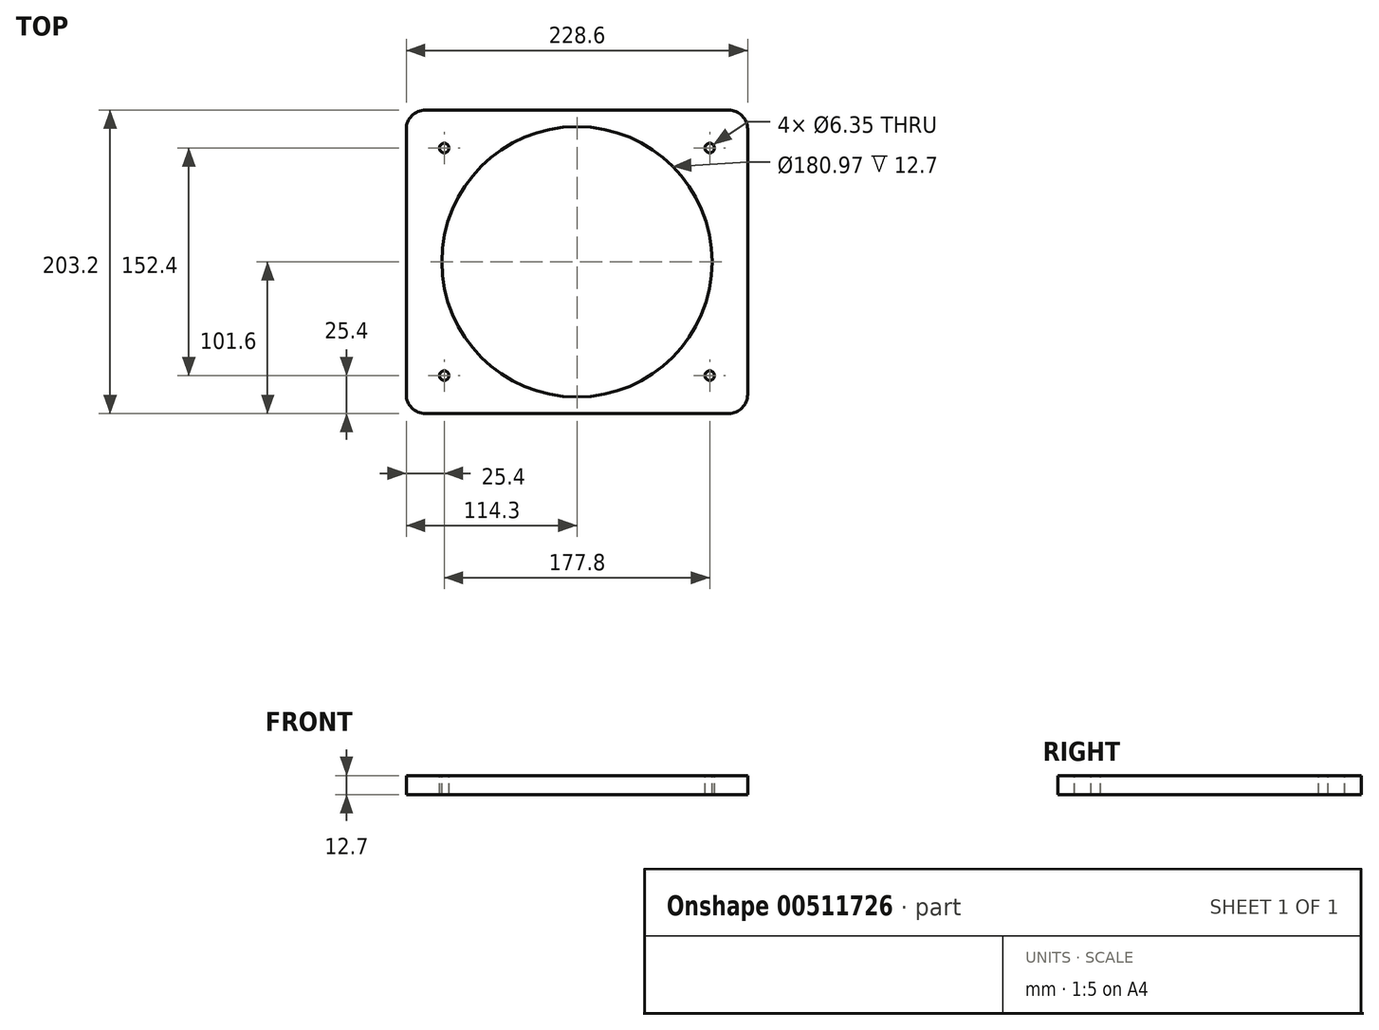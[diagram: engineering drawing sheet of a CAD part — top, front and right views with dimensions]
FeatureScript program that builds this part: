
annotation { "Feature Type Name" : "Feature", "Feature Type Description" : "" }
export const myFeature = defineFeature(function(context is Context, id is Id, definition is map)
    precondition{}
    {
        {
            var Q0;
            Q0=qCreatedBy(makeId("Top.planeOp"),FACE);
            var sketch = newSketch(context, id + "F0", { "sketchPlane" : qUnion([Q0])});
            skLineSegment(sketch, "E0.bottom", {"start": v(-101.6, 101.6) * mm, "end": v(101.6, 101.6) * mm});
            skLineSegment(sketch, "E0.top", {"start": v(-101.6, -101.6) * mm, "end": v(101.6, -101.6) * mm});
            skLineSegment(sketch, "E0.left", {"start": v(-114.3, 88.9) * mm, "end": v(-114.3, -88.9) * mm});
            skLineSegment(sketch, "E0.right", {"start": v(114.3, 88.9) * mm, "end": v(114.3, -88.9) * mm});
            skPoint(sketch, "E0.middle", {"position": v(0, 0) * mm});
            skPoint(sketch, "E1.visualSharp", {"position": v(-114.3, 101.6) * mm});
            skArc(sketch, "E1.filletArc", {"start": v(-101.6, 101.6) * mm, "mid": v(-110.58, 97.88) * mm, "end": v(-114.3, 88.9) * mm});
            skPoint(sketch, "E2.visualSharp", {"position": v(114.3, 101.6) * mm});
            skArc(sketch, "E2.filletArc", {"start": v(114.3, 88.9) * mm, "mid": v(110.58, 97.88) * mm, "end": v(101.6, 101.6) * mm});
            skPoint(sketch, "E3.visualSharp", {"position": v(-114.3, -101.6) * mm});
            skArc(sketch, "E3.filletArc", {"start": v(-114.3, -88.9) * mm, "mid": v(-110.58, -97.88) * mm, "end": v(-101.6, -101.6) * mm});
            skPoint(sketch, "E4.visualSharp", {"position": v(114.3, -101.6) * mm});
            skArc(sketch, "E4.filletArc", {"start": v(101.6, -101.6) * mm, "mid": v(110.58, -97.88) * mm, "end": v(114.3, -88.9) * mm});
            skSolve(sketch);
        }
        {
            var Q0;
            Q0=makeQuery(id+"F0.imprint","IMPRINT",FACE,{"disambiguationData":[TD([[makeQuery(id+"F0.imprint","IMPRINT",EDGE,{"derivedFrom":sQuery(id+"F0.wireOp",EDGE,"E0.bottom")}),-1.0]])]});
            extrude(context, id + "F1", {"entities" : qUnion([Q0]), "depth" : 12.7 * mm});
        }
        {
            var Q0;
            Q0=makeQuery(id+"F1.opExtrude","CAP_FACE",FACE,{"disambiguationData":[OSD([sQuery(id+"F0.wireOp",EDGE,"E0.bottom"),sQuery(id+"F0.wireOp",EDGE,"E0.top"),sQuery(id+"F0.wireOp",EDGE,"E0.left"),sQuery(id+"F0.wireOp",EDGE,"E0.right"),sQuery(id+"F0.wireOp",EDGE,"E1.filletArc"),sQuery(id+"F0.wireOp",EDGE,"E2.filletArc"),sQuery(id+"F0.wireOp",EDGE,"E3.filletArc"),sQuery(id+"F0.wireOp",EDGE,"E4.filletArc")])],"isStart":false});
            var sketch = newSketch(context, id + "F2", { "sketchPlane" : qUnion([Q0])});
            skCircle(sketch, "E5", {"center": v(0, 0) * mm, "radius": 90.49 * mm});
            skSolve(sketch);
        }
        {
            var Q0;
            Q0 = qSketchRegion(id + "F2", true);
            extrude(context, id + "F3", {"entities" : qUnion([Q0]), "operationType" : NewBodyOperationType.REMOVE, "oppositeDirection" : true, "depth" : 12.7 * mm});
        }
        {
            var Q0;
            Q0=makeQuery(id+"F1.opExtrude","CAP_FACE",FACE,{"disambiguationData":[OSD([sQuery(id+"F0.wireOp",EDGE,"E0.bottom"),sQuery(id+"F0.wireOp",EDGE,"E0.top"),sQuery(id+"F0.wireOp",EDGE,"E0.left"),sQuery(id+"F0.wireOp",EDGE,"E0.right"),sQuery(id+"F0.wireOp",EDGE,"E1.filletArc"),sQuery(id+"F0.wireOp",EDGE,"E2.filletArc"),sQuery(id+"F0.wireOp",EDGE,"E3.filletArc"),sQuery(id+"F0.wireOp",EDGE,"E4.filletArc")])],"isStart":false});
            var sketch = newSketch(context, id + "F4", { "sketchPlane" : qUnion([Q0])});
            skCircle(sketch, "E6", {"center": v(-88.9, -76.2) * mm, "radius": 2.54 * mm});
            skCircle(sketch, "E7.0.1.0", {"center": v(-88.9, 76.2) * mm, "radius": 2.54 * mm});
            skCircle(sketch, "E7.1.0.0", {"center": v(88.9, -76.2) * mm, "radius": 2.54 * mm});
            skCircle(sketch, "E7.1.1.0", {"center": v(88.9, 76.2) * mm, "radius": 2.54 * mm});
            skLineSegment(sketch, "E7.direction1", {"start": v(-88.9, -76.2) * mm, "end": v(88.9, -76.2) * mm, "construction": true});
            skLineSegment(sketch, "E7.direction2", {"start": v(-88.9, -76.2) * mm, "end": v(-88.9, 76.2) * mm, "construction": true});
            skSolve(sketch);
        }
        {
            var Q0;
            Q0=sQuery(id+"F4.wireOp",VERTEX,"E7.0.1.0.center");
            var Q1;
            Q1=sQuery(id+"F4.wireOp",VERTEX,"E7.1.1.0.center");
            var Q2;
            Q2=sQuery(id+"F4.wireOp",VERTEX,"E7.1.0.0.center");
            var Q3;
            Q3=sQuery(id+"F4.wireOp",VERTEX,"E6.center");
            var Q4;
            Q4=makeQuery(id+"F1.opExtrude","SWEPT_BODY",BODY,{"disambiguationData":[OSD([sQuery(id+"F0.wireOp",EDGE,"E0.bottom"),sQuery(id+"F0.wireOp",EDGE,"E0.top"),sQuery(id+"F0.wireOp",EDGE,"E0.left"),sQuery(id+"F0.wireOp",EDGE,"E0.right"),sQuery(id+"F0.wireOp",EDGE,"E1.filletArc"),sQuery(id+"F0.wireOp",EDGE,"E2.filletArc"),sQuery(id+"F0.wireOp",EDGE,"E3.filletArc"),sQuery(id+"F0.wireOp",EDGE,"E4.filletArc")])]});
            hole(context, id + "F5", {"style" : HoleStyle.SIMPLE, "endStyle" : HoleEndStyle.THROUGH, "holeDiameter" : 6.35 * mm, "isTappedThrough" : true, "tappedDepth" : 12.7 * mm, "tapClearance" : 3, "locations" : qUnion([Q0, Q1, Q2, Q3]), "scope" : qUnion([Q4])});
        }
    });
